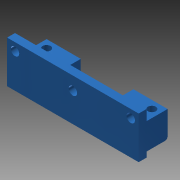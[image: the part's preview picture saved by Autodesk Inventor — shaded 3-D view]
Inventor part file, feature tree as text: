
AUTODESK INVENTOR PART (.ipt)
format: ipt  version: 2013 SP2 (Build 170200200, 200)  size: 145,408 bytes
history: native  units: mm
features: extrude x4, sketch x4, fillet x1
ambient origin geometry x8: Origin, YZ Plane, XZ Plane, XY Plane, X Axis, Y Axis, Z Axis, Center Point
bodies: Solid1 (feature_tree)
feature tree (9):
  extrude  "Extrusion1"  Depth=3.0mm
  extrude  "Extrusion2"  Depth=3.0mm
  extrude  "Extrusion3"  Depth=3.0mm
  fillet  "Fillet1"  Radius=40.0mm
  extrude  "Extrusion4"  Depth=6.0mm
  sketch  "Sketch1"  dims[d2=10.0mm d3=3.0mm]
  sketch  "Sketch2"  dims[d4=3.0mm d5=3.0mm]
  sketch  "Sketch3"  dims[d6=3.0mm d7=3.0mm d8=40.0mm]
  sketch  "Sketch4"  dims[d9=10.0mm d10=0.0mm d11=6.0mm d12=6.0mm d13=10.0mm d14=10.0mm d15=20.0mm d17=5.0mm d18=0.0mm d19=6.0mm d20=6.0mm d22=0.0mm d24=3.0mm d25=0.0mm d26=7.0mm d27=10.0mm d28=3.0mm d30=50.0mm d31=1.0mm d32=3.2mm d33=3.2mm d34=3.0mm d35=3.0mm d36=3.0mm d37=3.0mm d38=3.2mm d39=5.0mm d40=10.0mm d41=0.0mm]
